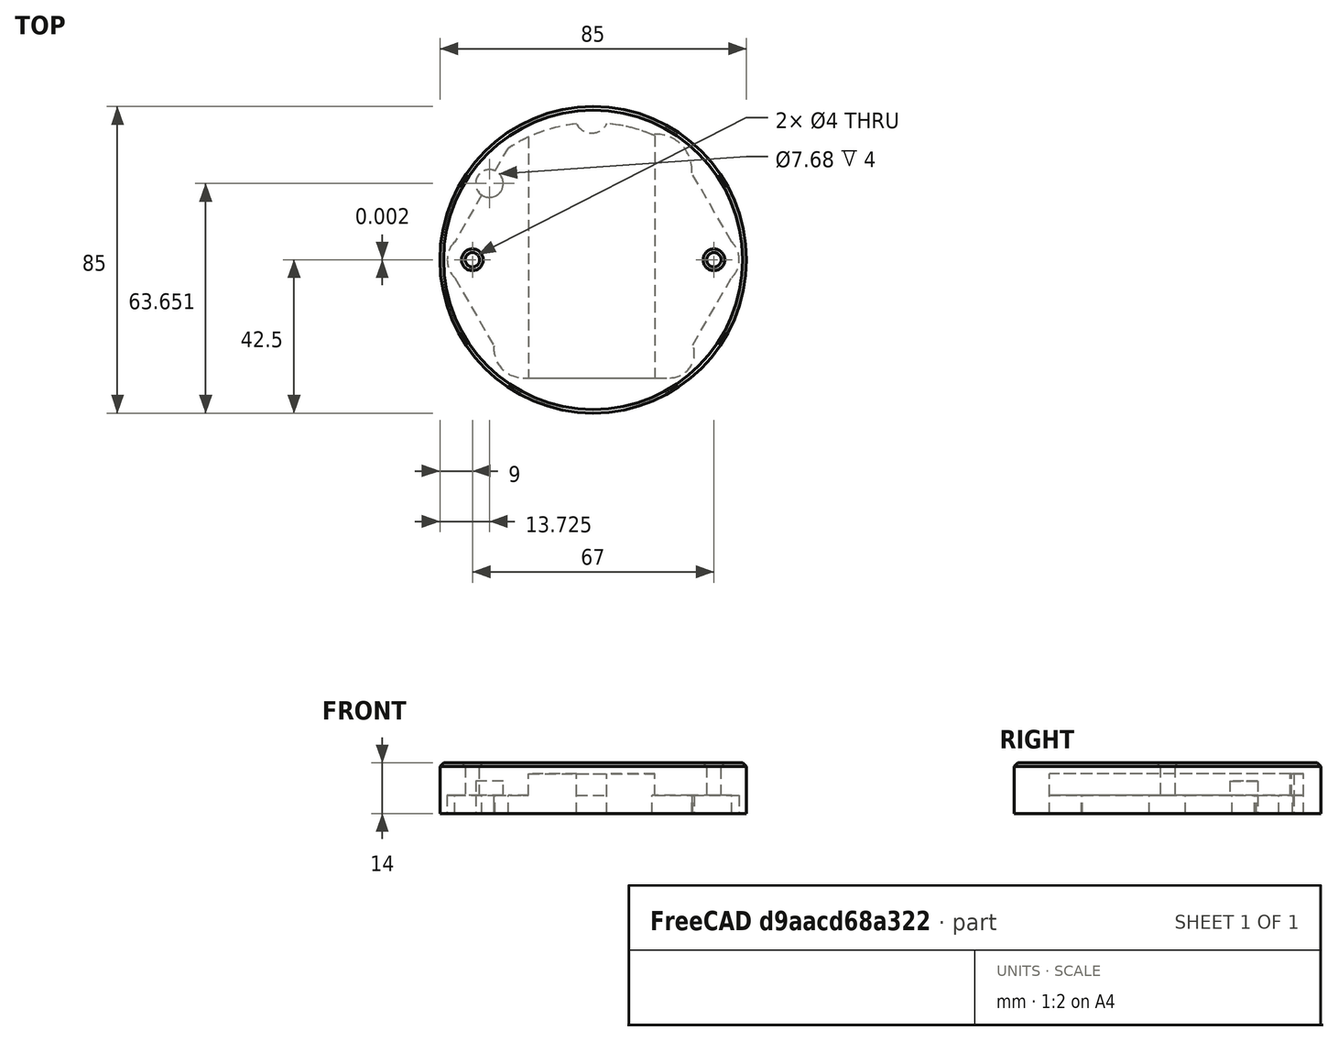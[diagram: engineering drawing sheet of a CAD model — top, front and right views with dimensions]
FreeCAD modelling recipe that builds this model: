
FCSTD DOCUMENT  (FreeCAD 0.20R29177 +426 (Git))
Label: Firby
License: All rights reserved
LicenseURL: http://en.wikipedia.org/wiki/All_rights_reserved
objects: Sketcher::SketchObject×5, PartDesign::Pad×3, PartDesign::Pocket×2, Image::ImagePlane×1, PartDesign::Chamfer×1, PartDesign::Body×1, Mesh::Feature×1
note: 18 computed .brp shape members not serialized (recipe doc carries the construction recipe); baked Part::Feature solids carry a one-line shape summary decoded from their .brp

FEATURE [Sketcher::SketchObject] Sketch
  FullyConstrained = false
  MapMode = 5
  Support = -> [XY_Plane]
  sketch-geometry (16):
    g0: Circle CenterX=0 CenterY=0 CenterZ=0 NormalX=0 NormalY=0 NormalZ=1 AngleXU=0 Radius=42.5
    g1: LineSegment StartX=38.399 StartY=5 StartZ=0 EndX=27.3401 EndY=24.1545 EndZ=0
    g2: LineSegment StartX=-30.9104 StartY=17.9614 StartZ=0 EndX=-38.4015 EndY=4.99934 EndZ=0
    g3: LineSegment StartX=-38.3981 StartY=-4.99911 StartZ=0 EndX=-27.5294 EndY=-23.8266 EndZ=0
    g4: LineSegment StartX=-19.4272 StartY=-32.7201 StartZ=0 EndX=21.3252 EndY=-32.7201 EndZ=0
    g5: LineSegment StartX=27.6573 StartY=-23.6051 StartZ=0 EndX=38.399 EndY=-5 EndZ=0
    g6: ArcOfCircle CenterX=33.5 CenterY=0 CenterZ=0 NormalX=0 NormalY=0 NormalZ=1 AngleXU=0 Radius=7 StartAngle=5.48758 EndAngle=7.07879
    g7: ArcOfCircle CenterX=-33.5 CenterY=0.00178244 CenterZ=0 NormalX=0 NormalY=0 NormalZ=1 AngleXU=0 Radius=7 StartAngle=2.34649 EndAngle=3.93738
    g8: ArcOfCircle CenterX=-19.4272 CenterY=-24.5827 CenterZ=0 NormalX=0 NormalY=0 NormalZ=1 AngleXU=0 Radius=8.13741 StartAngle=3.04855 EndAngle=4.71239
    g9: ArcOfCircle CenterX=21.3252 CenterY=-25.9632 CenterZ=0 NormalX=0 NormalY=0 NormalZ=1 AngleXU=0 Radius=6.75692 StartAngle=4.71239 EndAngle=6.63968
    g10: ArcOfCircle CenterX=-28.7752 CenterY=21.1512 CenterZ=0 NormalX=0 NormalY=0 NormalZ=1 AngleXU=0 Radius=3.83847 StartAngle=1.14866 EndAngle=4.12252
    g11: LineSegment StartX=-27.2025 StartY=24.6527 StartZ=0 EndX=-23.6004 EndY=30.8856 EndZ=0
    g12: ArcOfCircle CenterX=17.5628 CenterY=24.965 CenterZ=0 NormalX=0 NormalY=0 NormalZ=1 AngleXU=0 Radius=9.81084 StartAngle=6.20048 EndAngle=7.97472
    g13: ArcOfCircle CenterX=0 CenterY=-4.99624 CenterZ=0 NormalX=0 NormalY=0 NormalZ=1 AngleXU=0 Radius=42.9475 StartAngle=1.17946 EndAngle=1.48189
    g14: ArcOfCircle CenterX=0 CenterY=-4.99624 CenterZ=0 NormalX=0 NormalY=0 NormalZ=1 AngleXU=0 Radius=42.9475 StartAngle=1.67888 EndAngle=2.15258
    g15: ArcOfCircle CenterX=-0.429919 CenterY=39.8235 CenterZ=0 NormalX=0 NormalY=0 NormalZ=1 AngleXU=0 Radius=4.7088 StartAngle=3.60929 EndAngle=5.83467
  constraints (30):
    c: Coincident(g0,g-1)
    c: Diameter(g0) = 85
    c: Horizontal(g4)
    c: Distance(g6,g0) = 33.5
    c: Distance(g7,g0) = 33.5
    c: Diameter(g7) = 14
    c: Diameter(g6) = 14
    c: Coincident(g5,g6)
    c: Coincident(g6,g1)
    c: Coincident(g2,g7)
    c: Coincident(g7,g3)
    c: Coincident(g9,g5)
    c: Tangent(g9,g4) = -1.5708
    c: Tangent(g8,g4) = -1.5708
    c: Coincident(g10,g2)
    c: Coincident(g11,g10)
    c: Parallel(g11,g2)
    c: Coincident(g12,g1)
    c: Coincident(g14,g11)
    c: Block(g1)
    c: DistanceX(g10) = -27.2025
    c: DistanceY(g10) = 24.6527
    c: DistanceX(g11) = -23.6004
    c: DistanceY(g11) = 30.8856
    c: Coincident(g13,g12)
    c: Block(g12)
    c: Block(g13)
    c: Block(g14)
    c: Coincident(g15,g14)
    c: Coincident(g15,g13)
FEATURE [Image::ImagePlane] ImagePlane
  Placement = pos=(2,3.5,0) rot=(0,0,1;-0.02618rad)
  XSize = 167.61
  YSize = 223.481
FEATURE [PartDesign::Pad] Pad
  Direction = (0,0,1)
  Length = 5
  Length2 = 10
  Profile = -> Sketch
  ReferenceAxis = -> Sketch [N_Axis]
  Type = 0
FEATURE [Sketcher::SketchObject] Sketch001
  ExternalGeometry = -> [Pad]
  FullyConstrained = true
  MapMode = 5
  Placement = pos=(0,0,5) rot=(0,0,1;0rad)
  Support = -> [Pad]
  expr: Constraints[1] = Sketch.Constraints[1]
  sketch-geometry (7):
    g0: Circle CenterX=0 CenterY=0 CenterZ=0 NormalX=0 NormalY=0 NormalZ=1 AngleXU=0 Radius=42.5
    g1: LineSegment StartX=-17.9367 StartY=-32.7201 StartZ=0 EndX=17.0633 EndY=-32.7201 EndZ=0
    g2: ArcOfCircle CenterX=0 CenterY=-4.99624 CenterZ=0 NormalX=0 NormalY=0 NormalZ=1 AngleXU=0 Radius=42.9475 StartAngle=1.16222 EndAngle=1.4822
    g3: ArcOfCircle CenterX=-0.43674 CenterY=39.8237 CenterZ=0 NormalX=0 NormalY=0 NormalZ=1 AngleXU=0 Radius=4.7028 StartAngle=3.60998 EndAngle=5.83429
    g4: ArcOfCircle CenterX=0 CenterY=-4.99624 CenterZ=0 NormalX=0 NormalY=0 NormalZ=1 AngleXU=0 Radius=42.9475 StartAngle=1.67888 EndAngle=2.00165
    g5: LineSegment StartX=-17.9367 StartY=34.0263 StartZ=0 EndX=-17.9367 EndY=-32.7201 EndZ=0
    g6: LineSegment StartX=17.0633 StartY=34.4161 StartZ=0 EndX=17.0633 EndY=-32.7201 EndZ=0
  constraints (20):
    c: Coincident(g0,g-1)
    c: Diameter(g0) = 85
    c: Horizontal(g1)
    c: Coincident(g3,g2)
    c: Coincident(g5,g4)
    c: Coincident(g5,g1)
    c: Vertical(g5)
    c: Coincident(g6,g2)
    c: Coincident(g6,g1)
    c: Vertical(g6)
    c: Distance(g1) = 35
    c: DistanceX(g3) = -0.43674
    c: DistanceY(g3) = 39.8237
    c: Distance(g3,g6) = 17.5
    c: Coincident(g4,g3)
    c: Coincident(g3,g-4)
    c: PointOnObject(g-5,g2)
    c: Coincident(g-5,g4)
    c: Coincident(g2,g4)
    c: PointOnObject(g1,g-6)
FEATURE [PartDesign::Pad] Pad001
  BaseFeature = -> Pad
  Direction = (0,0,1)
  Length = 6
  Length2 = 10
  Profile = -> Sketch001
  ReferenceAxis = -> Sketch001 [N_Axis]
  Type = 0
FEATURE [Sketcher::SketchObject] Sketch002
  ExternalGeometry = -> [Pad001]
  FullyConstrained = true
  MapMode = 5
  Placement = pos=(0,0,11) rot=(0,0,1;0rad)
  Support = -> [Pad001]
  sketch-geometry (1):
    g0: Circle CenterX=0 CenterY=0 CenterZ=0 NormalX=0 NormalY=0 NormalZ=1 AngleXU=0 Radius=42.5
  constraints (2):
    c: Coincident(g0,g-3)
    c: Tangent(g0,g-3)
FEATURE [PartDesign::Pad] Pad002
  BaseFeature = -> Pad001
  Direction = (0,0,1)
  Length = 3
  Length2 = 10
  Profile = -> Sketch002
  ReferenceAxis = -> Sketch002 [N_Axis]
  Type = 0
FEATURE [Sketcher::SketchObject] Sketch003
  ExternalGeometry = -> [Pad002]
  FullyConstrained = true
  MapMode = 5
  Placement = pos=(0,0,5) rot=(1,0,0;3.14159rad)
  Support = -> [Pad002]
  sketch-geometry (1):
    g0: Circle CenterX=-28.7752 CenterY=-21.1512 CenterZ=0 NormalX=0 NormalY=0 NormalZ=1 AngleXU=0 Radius=3.83847
  constraints (2):
    c: Coincident(g0,g-3)
    c: PointOnObject(g-3,g0)
FEATURE [PartDesign::Pocket] Pocket
  BaseFeature = -> Pad002
  Direction = (0,0,1)
  Length = 4
  Length2 = 5
  Profile = -> Sketch003
  ReferenceAxis = -> Sketch003 [N_Axis]
  Type = 0
FEATURE [Sketcher::SketchObject] Sketch004
  ExternalGeometry = -> [Pocket]
  FullyConstrained = true
  MapMode = 5
  Placement = pos=(0,0,5) rot=(1,0,0;3.14159rad)
  Support = -> [Pocket]
  sketch-geometry (2):
    g0: Circle CenterX=-33.5 CenterY=-0.00178244 CenterZ=0 NormalX=0 NormalY=0 NormalZ=1 AngleXU=0 Radius=2
    g1: Circle CenterX=33.5 CenterY=0 CenterZ=0 NormalX=0 NormalY=0 NormalZ=1 AngleXU=0 Radius=2
  constraints (4):
    c: Coincident(g0,g-3)
    c: Coincident(g1,g-4)
    c: Diameter(g1) = 4
    c: Diameter(g0) = 4
FEATURE [PartDesign::Pocket] Pocket001
  BaseFeature = -> Pocket
  Direction = (0,0,1)
  Length = 10
  Length2 = 5
  Profile = -> Sketch004
  ReferenceAxis = -> Sketch004 [N_Axis]
  Type = 0
FEATURE [PartDesign::Chamfer] Chamfer
  Angle = 45
  Base = -> Pocket001 [Face27]
  BaseFeature = -> Pocket001
  ChamferType = 0
  FlipDirection = false
  Size = 1
  Size2 = 1
  SupportTransform = false
  UseAllEdges = false
FEATURE [PartDesign::Body] Body
  Group = -> [Sketch,Pad,Sketch001,Pad001,Sketch002,Pad002,Sketch003,Pocket,Sketch004,Pocket001,Chamfer]
  Origin = -> Origin
  Tip = -> Chamfer
FEATURE [Mesh::Feature] Mesh  label="Body (Meshed)"
